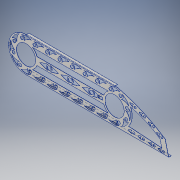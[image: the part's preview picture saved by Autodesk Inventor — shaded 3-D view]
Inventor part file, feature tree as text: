
AUTODESK INVENTOR PART (.ipt)
format: ipt  version: 2016 (Build 200138000, 138)  size: 862,208 bytes
history: native  units: in
note: dims shown in document units (in); Inventor stores cm internally (conversion verified against a paired STEP export)
features: sheet_metal_op x19, reference x9, other x9, sketch x7
ambient origin geometry x8: Origin, YZ Plane, XZ Plane, XY Plane, X Axis, Y Axis, Z Axis, Center Point
bodies: Solid1 (feature_tree)
feature tree (44):
  sheet_metal_op  "Face1"
  sheet_metal_op  "Flange3"
  sheet_metal_op  "Flange4"
  sheet_metal_op  "Flange5"
  sheet_metal_op  "Flange6"
  sheet_metal_op  "Flange7"
  sheet_metal_op  "Flange8"
  reference  "Reference3"
  reference  "Reference4"
  reference  "Reference5"
  reference  "Reference6"
  reference  "Reference7"
  reference  "Reference8"
  reference  "Reference9"
  reference  "Reference10"
  reference  "Reference11"
  other  "Plate1"
  sketch  "Sketch5"  dims[d1=0.2in]
  sketch  "Sketch6"  dims[d2=0.2in]
  other  "Plate4"
  sheet_metal_op  "Bend3"
  sheet_metal_op  "Corner3"
  sketch  "Sketch7"  dims[d10=0.8in]
  other  "Plate5"
  sheet_metal_op  "Bend4"
  sheet_metal_op  "Corner4"
  sketch  "Sketch8"  dims[d16=1.9685in d17=0.8in]
  other  "Plate6"
  sheet_metal_op  "Bend5"
  sheet_metal_op  "Corner5"
  sketch  "Sketch9"  dims[d36=5.0in]
  other  "Plate7"
  sheet_metal_op  "Bend6"
  sheet_metal_op  "Corner6"
  sketch  "Sketch10"  dims[d37=5.0in]
  other  "Plate8"
  sheet_metal_op  "Bend7"
  sheet_metal_op  "Corner7"
  sketch  "Sketch11"  dims[d42=1.0in d43=1.0in d44=3.0in d45=6.0in d46=1.0in d47=1.5in d57=1.9685in d59=0.7874in d61=0.7874in d62=1.9685in d64=180.0deg d66=1.9685in d68=180.0deg d70=2.7559in d72=3.25in d73=0.3937in d75=1.0in d77=2.7559in d79=3.25in d80=0.3937in d82=1.0in d87=3.2675in d89=0.6in d90=0.444in d92=0.7874in d94=0.7874in d96=1.9685in d98=1.9685in d100=2.7559in d102=0.3937in d104=2.7559in d106=0.3937in d110=0.7874in d112=0.7874in d114=1.9685in d116=1.9685in d118=2.7559in d120=0.3937in d122=2.7559in d124=0.3937in d128=0.7874in d130=0.7874in d132=1.9685in d134=1.9685in d136=2.7559in d138=0.3937in d140=2.7559in d142=0.3937in d146=0.7874in d148=0.7874in d150=1.9685in d152=1.9685in d154=2.7559in d156=0.3937in d158=2.7559in d160=0.3937in d164=0.7874in d166=0.7874in d168=1.9685in d170=1.9685in d172=2.7559in d174=0.3937in d176=2.7559in d178=0.3937in d182=0.7874in d184=0.7874in d186=1.9685in d188=1.9685in d190=2.7559in d192=0.3937in d194=2.7559in d196=0.3937in d200=0.7874in d202=0.7874in d204=1.9685in d206=1.9685in d208=2.7559in d210=0.3937in d212=2.7559in d214=0.3937in d218=0.7874in d220=0.7874in d222=1.9685in d224=1.9685in d226=2.7559in d228=0.3937in d230=2.7559in d232=0.3937in d233=0.6in d234=0.444in d236=0.7874in d238=0.7874in d240=1.9685in d242=1.9685in d244=2.7559in d246=0.3937in d248=2.7559in d250=0.3937in d251=0.6in d252=0.444in d254=0.7874in d256=0.7874in d258=1.9685in d260=1.9685in d262=2.7559in d264=0.3937in d266=2.7559in d268=0.3937in d269=0.6in d270=0.444in d272=0.7874in d274=0.7874in d276=1.9685in d278=1.9685in d280=2.7559in d282=0.3937in d284=2.7559in d286=0.3937in d287=0.6in d288=0.444in d290=0.7874in d292=0.7874in d294=1.9685in d296=1.9685in d298=2.7559in d300=0.3937in d302=2.7559in d304=0.3937in d305=0.6in d306=0.444in d308=0.7874in d310=0.7874in d312=1.9685in d314=1.9685in d316=2.7559in d318=0.3937in d320=2.7559in d322=0.3937in d323=0.6in d324=0.444in d326=0.7874in d328=0.7874in d330=1.9685in d332=1.9685in d334=2.7559in d336=0.3937in d338=2.7559in d340=0.3937in d341=0.6in d342=0.444in d344=0.7874in d346=0.7874in d348=1.9685in d350=1.9685in d352=2.7559in d354=0.3937in d356=2.7559in d358=0.3937in d360=0.064in d383=1.2in d384=0.064in d385=0.0in d386=0.0536in d387=0.064in d388=0.032in d389=0.128in d390=0.064in d391=0.75in d392=90.0deg d393=0.064in d394=0.256in d395=0.064in d396=0.064in d397=0.064in d398=0.032in d399=0.128in d400=0.064in d401=0.75in d402=90.0deg d403=0.064in d404=0.256in d405=0.064in d406=0.064in d407=0.064in d408=0.032in d409=0.128in d410=0.064in d411=0.75in d412=90.0deg d413=0.064in d414=0.256in d415=0.064in d416=0.064in d417=0.064in d418=0.032in d419=0.128in d420=0.064in d421=0.75in d422=90.0deg d423=0.064in d424=0.256in d425=0.064in d426=0.064in d427=0.064in d428=0.032in d429=0.128in d430=0.064in d431=0.75in d432=90.0deg d433=0.064in d434=0.256in d435=0.064in d436=0.064in d437=0.064in d438=0.032in d439=0.128in d440=0.064in d441=0.75in d442=90.0deg d443=0.064in d444=0.256in d445=0.064in d446=0.064in]
  other  "Plate9"
  sheet_metal_op  "Bend8"
  sheet_metal_op  "Corner8"
  other  "Cut1"
  other  "Definition1"
